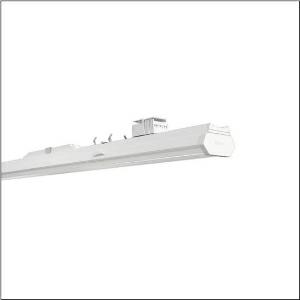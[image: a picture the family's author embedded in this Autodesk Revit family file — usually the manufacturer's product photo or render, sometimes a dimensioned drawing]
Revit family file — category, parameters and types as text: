
# Revit family: licross_r__11_protected_ho_51td12dn4fxm3c_9ee7
name_source: partatom
category: Lighting Fixtures
units: mm (PartAtom-declared; Revit-internal decimal feet)

## family parameters
Cut with Voids When Loaded = No
Host = Face
Light Source = No
Part Type = Normal
Room Calculation Point = No
Round Connector Dimension = Use Diameter
Shared = No

## types (1)
- --- (1 x LED, 970 lm, 7.4 W, 4000K)
    Apparent Load = 7 VA
    CIE Flux Codes = 70 91 97 98 100
    Color Rendering = 80
    Color Temperature = 4000K
    Default Elevation = 1800 mm
    Description = Licross® 11 Protected HO, luminaire insert, of sheet steel, galvanised, coil coated, white, length: 1.500mm, width: 90mm, height: 101mm, LED rated luminous flux: 15.270lm, light colour: 840, control gear: DALI 2 (for two DALI lines), with plug, 6-pole, with phase selection, for trunking rail, 14-core, mains connection: 220..240V, AC, 50/60Hz, rated input power: 91W, for trunking rail, 14-core, halogen-free wiring, for emergency light function, converter,control gear: single battery element, battery: LiFePO4, 9Ah, primary light control with lens, of plastic, primary optical cover: cover, of PMMA, light emission: direct distribution, primary light characteristic: symmetric, protection rating (complete): IP54, insulation class (complete): insulation class I (protective earthing), certification: CE, UKCA, protection symbol: D if used in an environment with non-conductive dust loads with corresponding accessories, impact resistance: IK06, permissible ambient temperature for indoor applications: +5..+30°C, standard: EN 60598-2-22, LABS conformity tested according to VDMA 24364:2018-05, reducing of maximum allowable ambient temperature of 5°C with ceiling mounting, corresponds to IFS (International Featured Standards) requirements for safety and quality in the food industry, packaging unit: 1 piece
    Height = 92 mm
    Lamp = 1 x LED
    Lamp Light Flux = 970 lm
    Lamp Power = 7.4 W
    Lamp count = 1
    Length = 1500 mm
    Luminous efficacy = 131 lm/W
    Manufacturer = Siteco
    ModVariant = No
    Model = 51TD12DN4FXM3C
    Mounting Place = Ceiling
    Mounting Type = Pendant
    Number of Poles = 1
    OnlyDefault = Yes
    Power Factor = 1
    Product Name = Licross® 11 Protected HO
    Product group = luminaire insert
    ProductGroupID = 902
    Protection Class = Protection class I
    Protection Degree = IP 54
    RLX_Detail_Level = 1
    RLX_Emergency_Light_Flux = 0 lm
    RLX_Emergency_Type = 0
    RLX_Emergency_Type_DB = No
    RlxData = <blob elided: 24989 chars, md5=ca6a43e2>
    Socket = socket
    Standby Power = 0 W
    System Light Flux = 970 lm
    System Power = 7 W
    Type Comments = : emergency light operation: 3 h
    Type Image = l_1256145.jpg
    URL = http://relux.com
    VarID = @adj_090862
    Voltage = 0 V
    Weight = 0.00 kg
    Width = 88 mm

## geometry (parser evidence)
native form markers: Blend x4, Sweep x10
no freeform markers — native parametric forms only
